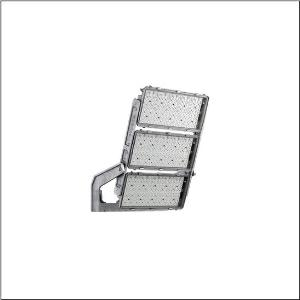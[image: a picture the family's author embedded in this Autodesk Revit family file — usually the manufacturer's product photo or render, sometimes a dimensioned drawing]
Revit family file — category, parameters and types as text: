
# Revit family: floodlight_fl_11_maxi_pro_remote___pl64_5xa779524e01aa_eec4
name_source: partatom
category: Lighting Fixtures
units: mm (PartAtom-declared; Revit-internal decimal feet)

## family parameters
Cut with Voids When Loaded = No
Host = Face
Light Source = No
Part Type = Normal
Room Calculation Point = No
Round Connector Dimension = Use Diameter
Shared = No

## types (1)
- --- (1 x LED, 128450 lm, 1334.7 W, 5700K)
    Apparent Load = 1335 VA
    CIE Flux Codes = 28 80 98 100 100
    Color Rendering = 90
    Color Temperature = 5700K
    Default Elevation = 1800 mm
    Description = Floodlight FL 11  maxi  pro Remote floodlight; light control with lens of PMMA; cover panel of toughened safety glass, transparent; light distribution: PL64, asymmetric direct distribution, LEDcolour temperature: 5700K, rated luminous flux: 128.450lm, colour rendering: CRI > 90, light colour: 957; luminous efficacy: 96lm/W; brightness control: DMX+RDM; with terminal, 6-pole, max. 2.5mm², mains connection: 220..240V/380..400V AC, 50/60Hz, surge voltage resistance: line to ground: 10kV, ECG replaceable separately, no afterglow with DALI off / DMX off command, LED unit replaceable without ESD environment, dustproof LED module, dimming range 10..100%; 1335W floodlight with 3x LED unit of diecast aluminium, coated grey; length: 713mm / width: 651mm / height: 338mm; mounting bracket, of diecast aluminium, uncoated, natural, equipment: Power, protection rating (complete): IP66; insulation class (complete): insulation class I (protective earthing); certification: CE, ENEC, VDE; ball protection: ball impact resistance with accessories, impact resistance: IK07; only for outdoor installations, rated ambient temperature 10°C, permissible operating ambient temperature: -40..+30°C, permissible storage temperature: -40..+85°C; packaging unit: 1 piece

Light Distribution: PL64
    Height = 320 mm
    Lamp = 1 x LED
    Lamp Light Flux = 128450 lm
    Lamp Power = 1334.7 W
    Lamp count = 1
    Length = 1002 mm
    Luminous efficacy = 96 lm/W
    Manufacturer = Siteco
    ModVariant = No
    Model = 5XA779524E01AA
    Mounting Place = Ceiling
    Mounting Type = Surface mounted
    Number of Poles = 1
    OnlyDefault = Yes
    Power Factor = 1
    Product Name = Floodlight FL 11 maxi pro Remote | PL64
    Product group = floodlight | ceiling mounted
    ProductGroupID = 303
    Protection Class = Protection class I
    Protection Degree = IP 66
    RLX_Detail_Level = 1
    RLX_Emergency_Light_Flux = 0 lm
    RLX_Emergency_Type = 0
    RLX_Emergency_Type_DB = No
    RlxData = <blob elided: 52437 chars, md5=d6d50b8f>
    Socket = socket
    Standby Power = 0 W
    System Light Flux = 128450 lm
    System Power = 1335 W
    Type Comments = factory setting: luminous flux: 100 % | dim-lin: 255 | 920 mA
    Type Image = l_1006784.jpg
    URL = http://relux.com
    VarID = @adj_045761
    Voltage = 0 V
    Weight = 0.00 kg
    Width = 655 mm

## geometry (parser evidence)
native form markers: Blend x4, Sweep x12
no freeform markers — native parametric forms only
